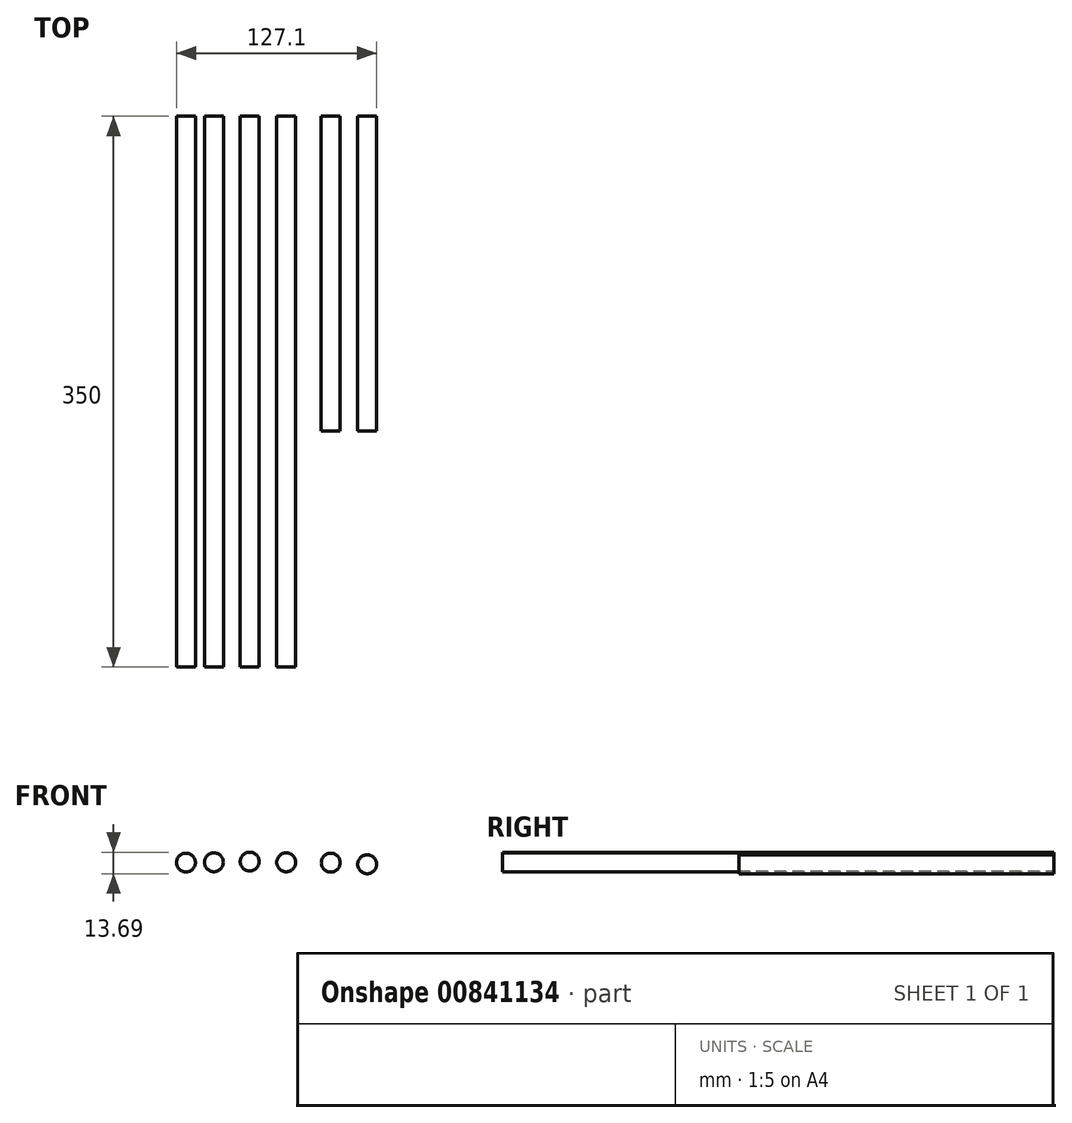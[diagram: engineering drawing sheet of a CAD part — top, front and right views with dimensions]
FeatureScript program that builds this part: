
annotation { "Feature Type Name" : "Feature", "Feature Type Description" : "" }
export const myFeature = defineFeature(function(context is Context, id is Id, definition is map)
    precondition{}
    {
        {
            var Q0;
            Q0=qCreatedBy(makeId("Front.planeOp"),FACE);
            var sketch = newSketch(context, id + "F0", { "sketchPlane" : qUnion([Q0])});
            skCircle(sketch, "E0", {"center": v(-58.45, 41.55) * mm, "radius": 6 * mm});
            skCircle(sketch, "E1", {"center": v(-76.16, 41.34) * mm, "radius": 6 * mm});
            skCircle(sketch, "E2", {"center": v(-35.68, 41.97) * mm, "radius": 6 * mm});
            skCircle(sketch, "E3", {"center": v(-12.54, 41.5) * mm, "radius": 6 * mm});
            skCircle(sketch, "E4", {"center": v(15.77, 41.31) * mm, "radius": 6 * mm});
            skCircle(sketch, "E5", {"center": v(38.94, 40.28) * mm, "radius": 6 * mm});
            skSolve(sketch);
        }
        {
            var Q0;
            Q0=makeQuery(id+"F0.imprint","IMPRINT",FACE,{"disambiguationData":[TD([[makeQuery(id+"F0.imprint","IMPRINT",EDGE,{"derivedFrom":sQuery(id+"F0.wireOp",EDGE,"E1")}),1.0]])]});
            var Q1;
            Q1=makeQuery(id+"F0.imprint","IMPRINT",FACE,{"disambiguationData":[TD([[makeQuery(id+"F0.imprint","IMPRINT",EDGE,{"derivedFrom":sQuery(id+"F0.wireOp",EDGE,"E0")}),1.0]])]});
            var Q2;
            Q2=makeQuery(id+"F0.imprint","IMPRINT",FACE,{"disambiguationData":[TD([[makeQuery(id+"F0.imprint","IMPRINT",EDGE,{"derivedFrom":sQuery(id+"F0.wireOp",EDGE,"E2")}),1.0]])]});
            var Q3;
            Q3=makeQuery(id+"F0.imprint","IMPRINT",FACE,{"disambiguationData":[TD([[makeQuery(id+"F0.imprint","IMPRINT",EDGE,{"derivedFrom":sQuery(id+"F0.wireOp",EDGE,"E3")}),1.0]])]});
            extrude(context, id + "F1", {"entities" : qUnion([Q0, Q1, Q2, Q3]), "depth" : 350 * mm, "offsetDistance" : 25 * mm});
        }
        {
            var Q0;
            Q0=makeQuery(id+"F0.imprint","IMPRINT",FACE,{"disambiguationData":[TD([[makeQuery(id+"F0.imprint","IMPRINT",EDGE,{"derivedFrom":sQuery(id+"F0.wireOp",EDGE,"E4")}),1.0]])]});
            var Q1;
            Q1=makeQuery(id+"F0.imprint","IMPRINT",FACE,{"disambiguationData":[TD([[makeQuery(id+"F0.imprint","IMPRINT",EDGE,{"derivedFrom":sQuery(id+"F0.wireOp",EDGE,"E5")}),1.0]])]});
            extrude(context, id + "F2", {"entities" : qUnion([Q0, Q1]), "depth" : 200 * mm, "offsetDistance" : 25 * mm});
        }
    });
